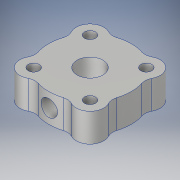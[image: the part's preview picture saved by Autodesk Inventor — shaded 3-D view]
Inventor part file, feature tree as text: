
AUTODESK INVENTOR PART (.ipt)
format: ipt  version: 2019 (Build 230136000, 136)  size: 160,768 bytes
history: native  units: in
note: dims shown in document units (in); Inventor stores cm internally (conversion verified against a paired STEP export)
features: fillet x1
ambient origin geometry x8: Origin, YZ Plane, XZ Plane, XY Plane, X Axis, Y Axis, Z Axis, Center Point
bodies: Solid1 (feature_tree)
feature tree (1):
  fillet  "Fillet1"  [1 undecoded]
note: 1 required parameter value undecoded (feature->parameter linkage not recoverable at this tier; creation-order binding heuristic only, values carry confidence <= 0.55)
